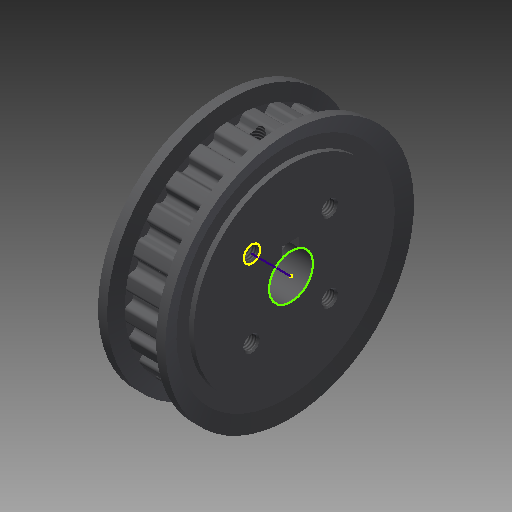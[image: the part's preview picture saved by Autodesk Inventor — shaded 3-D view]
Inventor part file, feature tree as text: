
AUTODESK INVENTOR PART (.ipt)
format: ipt  version: 2017 (Build 210142000, 142)  size: 600,576 bytes
history: native  units: mm
features: other x14, revolve x4, sketch x3, hole x2, extrude x2, thread x2, pattern_linear x1
ambient origin geometry x8: Origin, YZ Plane, XZ Plane, XY Plane, X Axis, Y Axis, Z Axis, Center Point
bodies: Solid1 (feature_tree)
feature tree (28):
  revolve  "Revolution1"  [1 undecoded]
  hole  "Hole1"  [1 undecoded]
  extrude  "Extrusion1"  TaperAngle=360.0deg  [1 undecoded]
  extrude  "Extrusion2"  TaperAngle=360.0deg  [1 undecoded]
  revolve  "Revolution2"  [1 undecoded]
  revolve  "Revolution3"  Angle=360.0deg
  thread  "Thread1"  [1 undecoded]
  revolve  "Revolution4"  [1 undecoded]
  thread  "Thread2"  [1 undecoded]
  hole  "Hole2"  [1 undecoded]
  pattern_linear  "Rectangular Pattern1"  [2 undecoded]
  other  "to_screw1_XY"
  other  "to_screw1_YZ"
  other  "to_screw1_ZX"
  other  "to_screw1_X"
  other  "to_screw1_Y"
  other  "to_screw1_Z"
  other  "to_screw1_Center"
  other  "to_screw2_XY"
  other  "to_screw2_YZ"
  other  "to_screw2_ZX"
  other  "to_screw2_X"
  other  "to_screw2_Y"
  other  "to_screw2_Z"
  other  "to_screw2_Center"
  sketch  "스케치9"
  sketch  "Sketch2"  dims[d0=360.0deg]
  sketch  "Sketch8"  dims[d1=8.0mm d2=6.0mm d3=4.0mm d4=2.0mm d5=90.0deg d6=12.5mm d7=0.0mm d8=7.5mm d9=0.0mm d10=12.5mm d11=0.0mm d12=360.0deg d13=360.0deg d14=14.56mm d15=0.0mm d16=360.0deg d17=15.96mm d18=0.0mm d19=2.459mm d20=6.2705mm d21=3.0mm d22=2.0mm d23=90.0deg d24=8.790148mm d25=120.0deg d26=20.0mm d28=14.142136mm d29=20.0mm d31=14.142136mm d32=0.0mm]
note: 11 required parameter values undecoded (feature->parameter linkage not recoverable at this tier; creation-order binding heuristic only, values carry confidence <= 0.55)